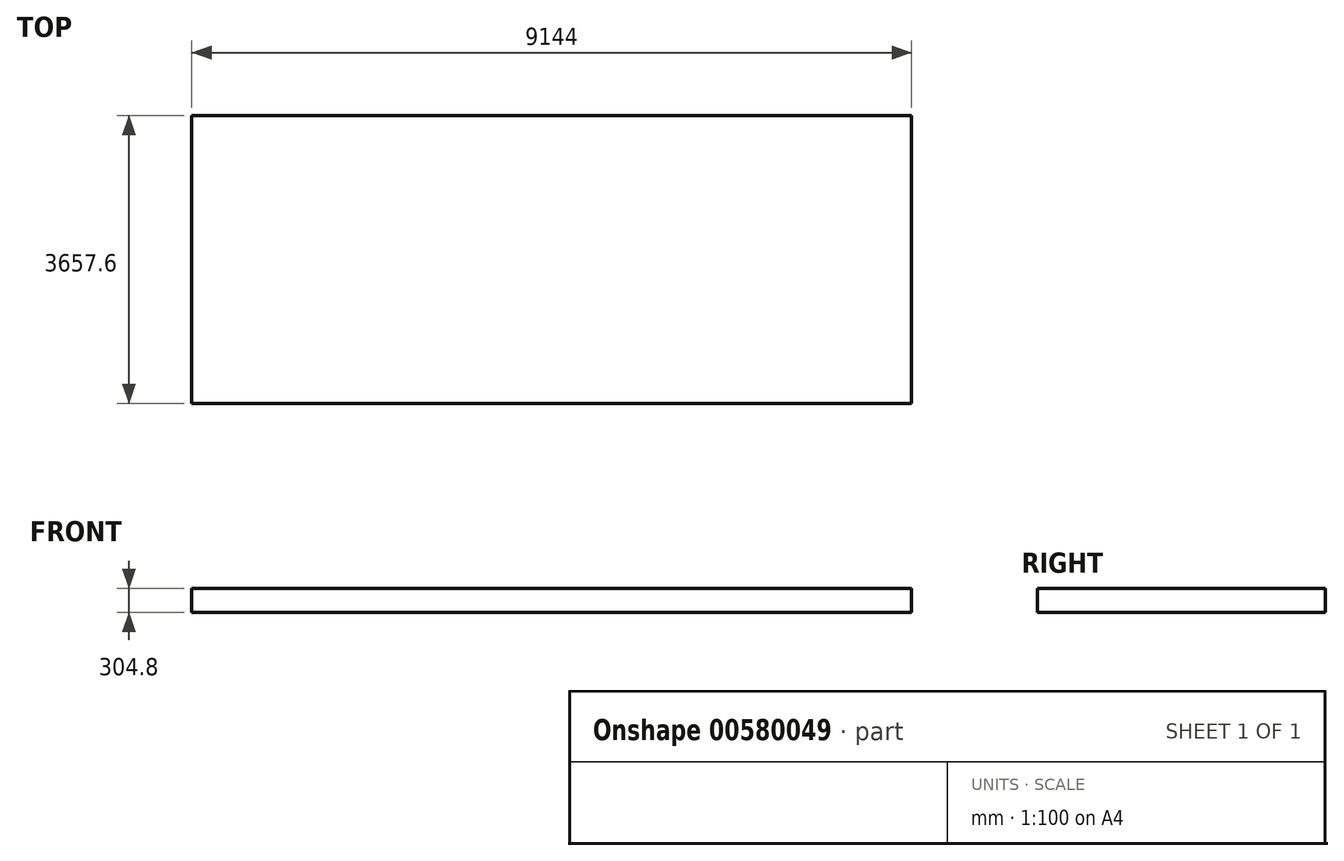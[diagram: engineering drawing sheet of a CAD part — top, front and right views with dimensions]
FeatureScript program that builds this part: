
annotation { "Feature Type Name" : "Feature", "Feature Type Description" : "" }
export const myFeature = defineFeature(function(context is Context, id is Id, definition is map)
    precondition{}
    {
        {
            var Q0;
            Q0=qCreatedBy(makeId("Top.planeOp"),FACE);
            var sketch = newSketch(context, id + "F0", { "sketchPlane" : qUnion([Q0])});
            skLineSegment(sketch, "E0.bottom", {"start": v(-4575.74, 1348.45) * mm, "end": v(4568.26, 1348.45) * mm});
            skLineSegment(sketch, "E0.top", {"start": v(-4575.74, -2309.15) * mm, "end": v(4568.26, -2309.15) * mm});
            skLineSegment(sketch, "E0.left", {"start": v(-4575.74, 1348.45) * mm, "end": v(-4575.74, -2309.15) * mm});
            skLineSegment(sketch, "E0.right", {"start": v(4568.26, 1348.45) * mm, "end": v(4568.26, -2309.15) * mm});
            skSolve(sketch);
        }
        {
            var Q0;
            Q0 = qSketchRegion(id + "F0", true);
            extrude(context, id + "F1", {"entities" : qUnion([Q0]), "depth" : 304.8 * mm, "offsetDistance" : 30.48 * mm});
        }
    });
